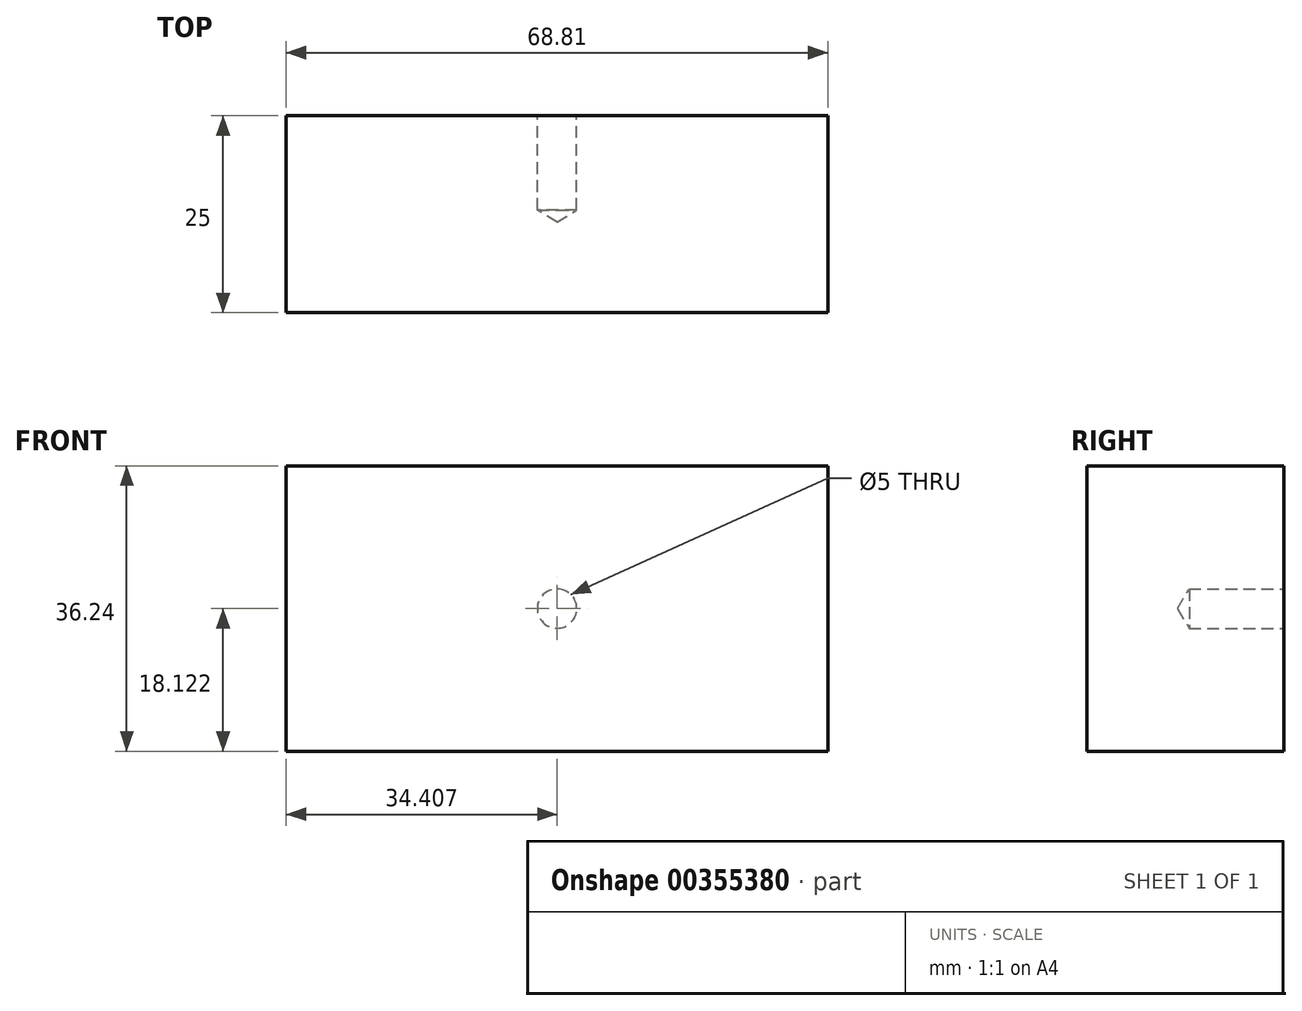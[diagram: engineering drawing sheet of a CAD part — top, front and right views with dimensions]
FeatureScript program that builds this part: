
annotation { "Feature Type Name" : "Feature", "Feature Type Description" : "" }
export const myFeature = defineFeature(function(context is Context, id is Id, definition is map)
    precondition{}
    {
        {
            var Q0;
            Q0=qCreatedBy(makeId("Front.planeOp"),FACE);
            var sketch = newSketch(context, id + "F0", { "sketchPlane" : qUnion([Q0])});
            skLineSegment(sketch, "E0.bottom", {"start": v(0, 28.42) * mm, "end": v(-68.8, 28.42) * mm});
            skLineSegment(sketch, "E0.top", {"start": v(0, 64.66) * mm, "end": v(-68.8, 64.66) * mm});
            skLineSegment(sketch, "E0.left", {"start": v(0, 28.42) * mm, "end": v(0, 64.66) * mm});
            skLineSegment(sketch, "E0.right", {"start": v(-68.8, 28.42) * mm, "end": v(-68.8, 64.66) * mm});
            skPoint(sketch, "E0.middle", {"position": v(-34.4, 46.54) * mm});
            skCircle(sketch, "E1", {"center": v(-58.23, -28.27) * mm, "radius": 48.03 * mm});
            skCircle(sketch, "E2", {"center": v(122.67, 53.86) * mm, "radius": 47.4 * mm});
            skSolve(sketch);
        }
        {
            var Q0;
            Q0=makeQuery(id+"F0.imprint","IMPRINT",FACE,{"disambiguationData":[TD([[makeQuery(id+"F0.imprint","IMPRINT",EDGE,{"derivedFrom":sQuery(id+"F0.wireOp",EDGE,"E0.bottom")}),-1.0]])]});
            extrude(context, id + "F1", {"entities" : qUnion([Q0]), "depth" : 25 * mm});
        }
        {
            var Q0;
            Q0=sQuery(id+"F0.wireOp",VERTEX,"E0.middle");
            var Q1;
            Q1=makeQuery(id+"F1.opExtrude","SWEPT_BODY",BODY,{"disambiguationData":[OSD([sQuery(id+"F0.wireOp",EDGE,"E0.bottom"),sQuery(id+"F0.wireOp",EDGE,"E0.top"),sQuery(id+"F0.wireOp",EDGE,"E0.left"),sQuery(id+"F0.wireOp",EDGE,"E0.right")])]});
            hole(context, id + "F2", {"style" : HoleStyle.SIMPLE, "endStyle" : HoleEndStyle.BLIND, "oppositeDirection" : true, "holeDiameter" : 5 * mm, "holeDepth" : 12 * mm, "isTappedThrough" : true, "tappedDepth" : 12 * mm, "tapClearance" : 3, "locations" : qUnion([Q0]), "scope" : qUnion([Q1])});
        }
    });
